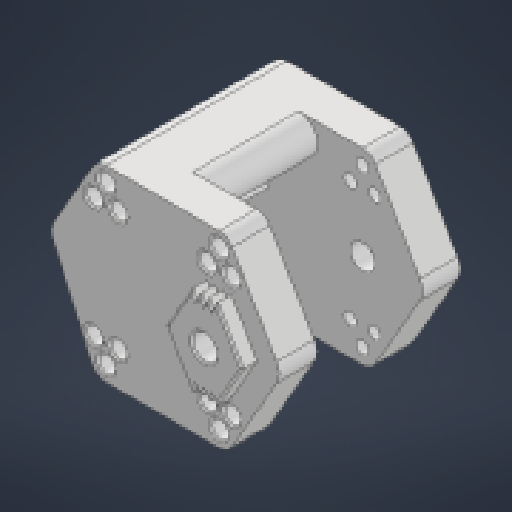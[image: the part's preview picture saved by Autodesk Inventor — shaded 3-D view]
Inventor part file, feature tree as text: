
AUTODESK INVENTOR PART (.ipt)
format: ipt  version: 2024.1 (Build 281209000, 209)  size: 435,200 bytes
history: native  units: in
note: dims shown in document units (in); Inventor stores cm internally (conversion verified against a paired STEP export)
features: extrude x6, other x3, chamfer x2, sketch x1, mirror x1, fillet x1, reference x1
ambient origin geometry x8: Origin, YZ Plane, XZ Plane, XY Plane, X Axis, Y Axis, Z Axis, Center Point
bodies: Solid1 (feature_tree)
feature tree (15):
  sketch  "Sketch1"  dims[d0=0.219in d1=0.219in d2=0.1654in d3=0.1654in d4=0.2in d5=0.2in d6=0.219in d7=0.1654in d8=0.25in d9=0.4in d10=0.3268in d11=0.5906in d12=0.5in d13=0.0in d14=0.2in d15=0.0in d16=0.2488in d17=0.5in d18=0.0in d19=0.0in d20=4.0in d21=0.0in d22=0.2756in d23=0.0in d24=0.025in d25=0.125in d26=45.0deg d27=2.0in d29=0.75in d30=1.0in d31=45.0deg d32=0.7874in d34=1.5in d35=0.3937in d37=1.0in d39=0.4in d40=0.4in d42=0.05in d43=1.1998in d44=0.0in d45=0.25in d46=0.025in d47=0.125in d48=45.0deg]
  extrude  "Extrusion1"  Depth=0.25in
  extrude  "Extrusion2"  Depth=0.25in
  extrude  "Extrusion3"  Depth=0.25in
  extrude  "Extrusion6"  Depth=0.2in
  extrude  "Extrusion4"  Depth=0.2in
  extrude  "Extrusion5"  Depth=0.25in
  chamfer  "Chamfer1"  Distance=0.1654in
  mirror  "Mirror1"
  fillet  "Fillet1"  Radius=0.25in
  chamfer  "Chamfer2"  Distance=0.4in
  reference  "Reference1"
  other  "<userpath>\Documents\School\FallCAD\Trebuchet\Trebuchet.iam"
  other  "Trebuchet.iam"
  other  "WeightArm:1"
